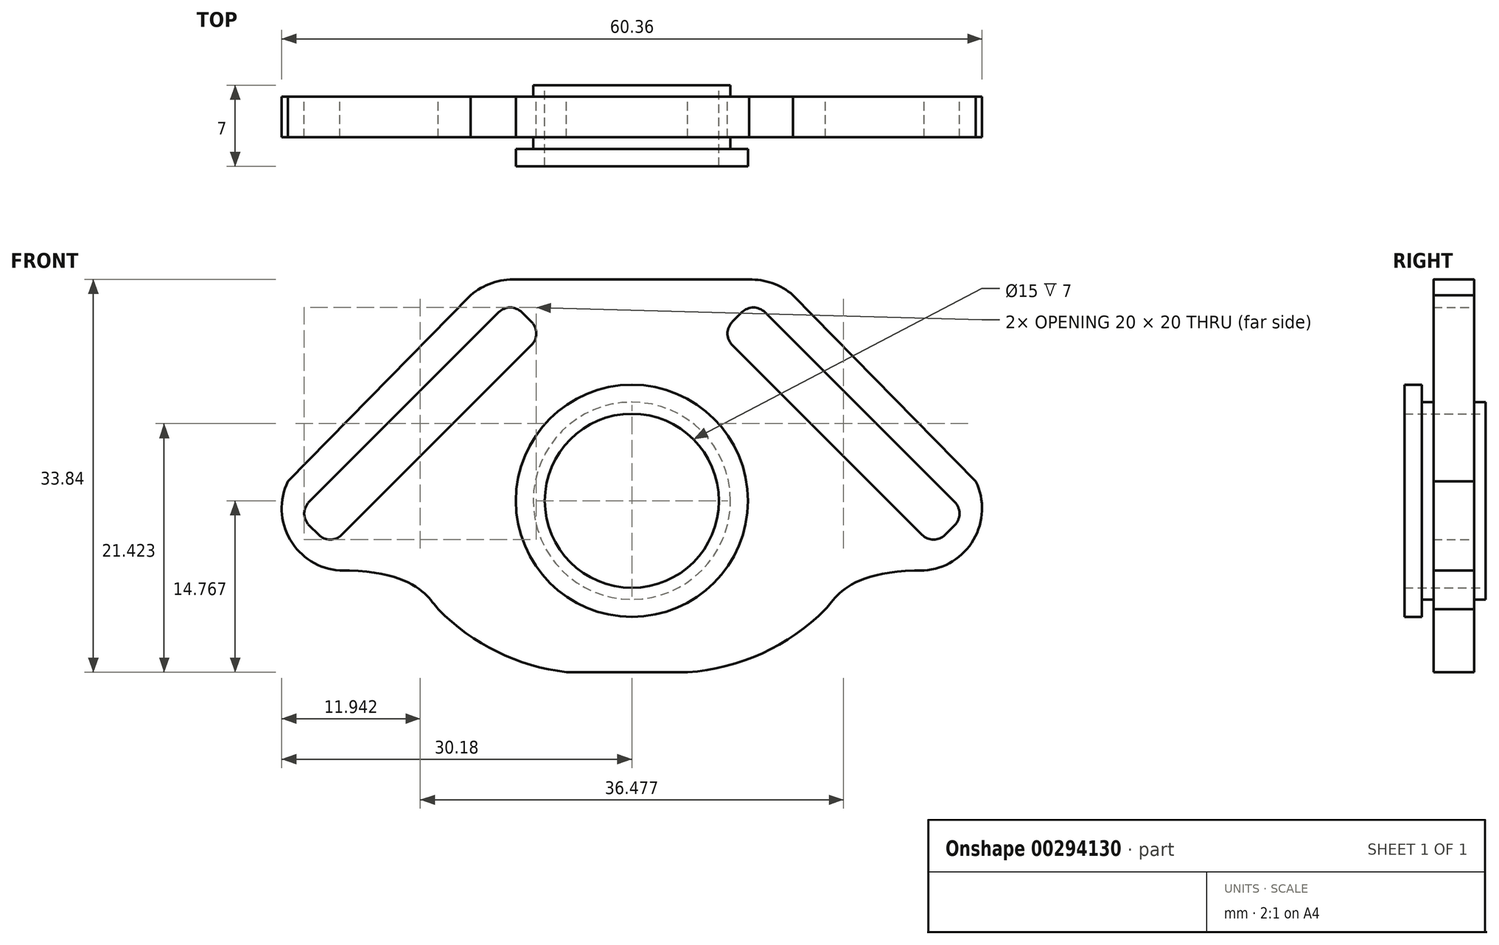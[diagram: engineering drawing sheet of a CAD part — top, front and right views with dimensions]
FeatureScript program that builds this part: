
annotation { "Feature Type Name" : "Feature", "Feature Type Description" : "" }
export const myFeature = defineFeature(function(context is Context, id is Id, definition is map)
    precondition{}
    {
        {
            var Q0;
            Q0=qCreatedBy(makeId("Front.planeOp"),FACE);
            var sketch = newSketch(context, id + "F0", { "sketchPlane" : qUnion([Q0])});
            skLineSegment(sketch, "E0.0", {"start": v(-29.64, 0) * mm, "end": v(-13.9, 16.05) * mm});
            skLineSegment(sketch, "E1.0", {"start": v(11.47, 14.57) * mm, "end": v(27.82, -1.78) * mm});
            skLineSegment(sketch, "E2.0", {"start": v(25, -4.6) * mm, "end": v(8.65, 11.75) * mm});
            skLineSegment(sketch, "E3.0", {"start": v(-25, -4.6) * mm, "end": v(-8.65, 11.75) * mm});
            skLineSegment(sketch, "E4.0", {"start": v(-11.47, 14.57) * mm, "end": v(-27.82, -1.78) * mm});
            skLineSegment(sketch, "E5.0", {"start": v(-8.65, 13.74) * mm, "end": v(-9.48, 14.57) * mm});
            skLineSegment(sketch, "E6.0", {"start": v(-27.82, -3.77) * mm, "end": v(-27, -4.6) * mm});
            skLineSegment(sketch, "E7.0", {"start": v(8.65, 13.74) * mm, "end": v(9.48, 14.57) * mm});
            skLineSegment(sketch, "E8.0", {"start": v(27.82, -3.77) * mm, "end": v(27, -4.6) * mm});
            skArc(sketch, "E9", {"start": v(13.9, 16.05) * mm, "mid": v(12.11, 17.07) * mm, "end": v(10.09, 17.4) * mm});
            skArc(sketch, "E10", {"start": v(11.47, 14.57) * mm, "mid": v(10.48, 14.98) * mm, "end": v(9.48, 14.57) * mm});
            skArc(sketch, "E11", {"start": v(8.65, 13.74) * mm, "mid": v(8.24, 12.74) * mm, "end": v(8.65, 11.75) * mm});
            skArc(sketch, "E12", {"start": v(27.82, -3.77) * mm, "mid": v(28.24, -2.78) * mm, "end": v(27.82, -1.78) * mm});
            skArc(sketch, "E13", {"start": v(25, -4.6) * mm, "mid": v(26, -5.01) * mm, "end": v(27, -4.6) * mm});
            skArc(sketch, "E14", {"start": v(4.82, -16.44) * mm, "mid": v(11.24, -14.81) * mm, "end": v(16.68, -11.02) * mm});
            skArc(sketch, "E15.MirrorCS", {"start": v(-8.65, 13.74) * mm, "mid": v(-8.24, 12.74) * mm, "end": v(-8.65, 11.75) * mm});
            skArc(sketch, "E16.MirrorCS", {"start": v(-11.47, 14.57) * mm, "mid": v(-10.48, 14.98) * mm, "end": v(-9.48, 14.57) * mm});
            skArc(sketch, "E17.MirrorCS", {"start": v(-27.82, -3.77) * mm, "mid": v(-28.24, -2.78) * mm, "end": v(-27.82, -1.78) * mm});
            skArc(sketch, "E18.MirrorCS", {"start": v(-25, -4.6) * mm, "mid": v(-26, -5.01) * mm, "end": v(-27, -4.6) * mm});
            skArc(sketch, "E19.MirrorCS", {"start": v(-25.18, -7.68) * mm, "mid": v(-29.45, -5.03) * mm, "end": v(-29.64, 0) * mm});
            skFitSpline(sketch, "E20.MirrorCS", {"points": [v(-25.18, -7.68) * mm, v(-16.68, -11.02) * mm], "startDerivative": vector(19.86, 0.13) * mm, "endDerivative": vector(2.7, -2.88) * mm});
            skArc(sketch, "E21.MirrorCS", {"start": v(-5.64, -16.44) * mm, "mid": v(-11.62, -14.68) * mm, "end": v(-16.68, -11.02) * mm});
            skArc(sketch, "E22.MirrorCS", {"start": v(-13.9, 16.05) * mm, "mid": v(-12.06, 17.09) * mm, "end": v(-9.98, 17.4) * mm});
            skCircle(sketch, "E23", {"center": v(0, -1.67) * mm, "radius": 7.5 * mm});
            skPoint(sketch, "E24", {"position": v(-9.98, 17.4) * mm});
            skPoint(sketch, "E25", {"position": v(10.09, 17.4) * mm});
            skLineSegment(sketch, "E26", {"start": v(-9.98, 17.4) * mm, "end": v(10.09, 17.4) * mm});
            skLineSegment(sketch, "E27.MirrorCS", {"start": v(29.64, 0) * mm, "end": v(13.9, 16.05) * mm});
            skArc(sketch, "E28.MirrorCS", {"start": v(25.18, -7.68) * mm, "mid": v(29.45, -5.03) * mm, "end": v(29.64, 0) * mm});
            skFitSpline(sketch, "E29.MirrorCS", {"points": [v(25.18, -7.68) * mm, v(16.68, -11.02) * mm], "startDerivative": vector(-19.86, 0.13) * mm, "endDerivative": vector(-2.7, -2.88) * mm});
            skLineSegment(sketch, "E30", {"start": v(-5.64, -16.44) * mm, "end": v(4.82, -16.44) * mm});
            skSolve(sketch);
        }
        {
            var Q0;
            Q0=makeQuery(id+"F0.imprint","IMPRINT",FACE,{"disambiguationData":[TD([[makeQuery(id+"F0.imprint","IMPRINT",EDGE,{"derivedFrom":sQuery(id+"F0.wireOp",EDGE,"E0.0")}),-1.0]])]});
            extrude(context, id + "F1", {"entities" : qUnion([Q0]), "endBound" : BoundingType.SYMMETRIC, "depth" : 3.5 * mm});
        }
        {
            var Q0;
            Q0=qCreatedBy(makeId("Front.planeOp"),FACE);
            var sketch = newSketch(context, id + "F2", { "sketchPlane" : qUnion([Q0])});
            skCircle(sketch, "E31.0", {"center": v(0, -1.67) * mm, "radius": 8.5 * mm});
            skCircle(sketch, "E32.0", {"center": v(0, -1.67) * mm, "radius": 7.5 * mm});
            skSolve(sketch);
        }
        {
            var Q0;
            Q0 = qSketchRegion(id + "F2", true);
            extrude(context, id + "F3", {"entities" : qUnion([Q0]), "operationType" : NewBodyOperationType.ADD, "endBound" : BoundingType.SYMMETRIC, "depth" : 5.5 * mm});
        }
        {
            var Q0;
            Q0=makeQuery(id+"F3.opExtrude","CAP_FACE",FACE,{"disambiguationData":[OSD([sQuery(id+"F2.wireOp",EDGE,"E31.0"),sQuery(id+"F2.wireOp",EDGE,"E32.0")])],"isStart":false});
            var sketch = newSketch(context, id + "F4", { "sketchPlane" : qUnion([Q0])});
            skCircle(sketch, "E33.0", {"center": v(0, -1.67) * mm, "radius": 10 * mm});
            skCircle(sketch, "E34.0", {"center": v(0, -1.67) * mm, "radius": 7.5 * mm});
            skSolve(sketch);
        }
        {
            var Q0;
            Q0 = qSketchRegion(id + "F4", true);
            extrude(context, id + "F5", {"entities" : qUnion([Q0]), "operationType" : NewBodyOperationType.ADD, "depth" : 1.5 * mm});
        }
    });
